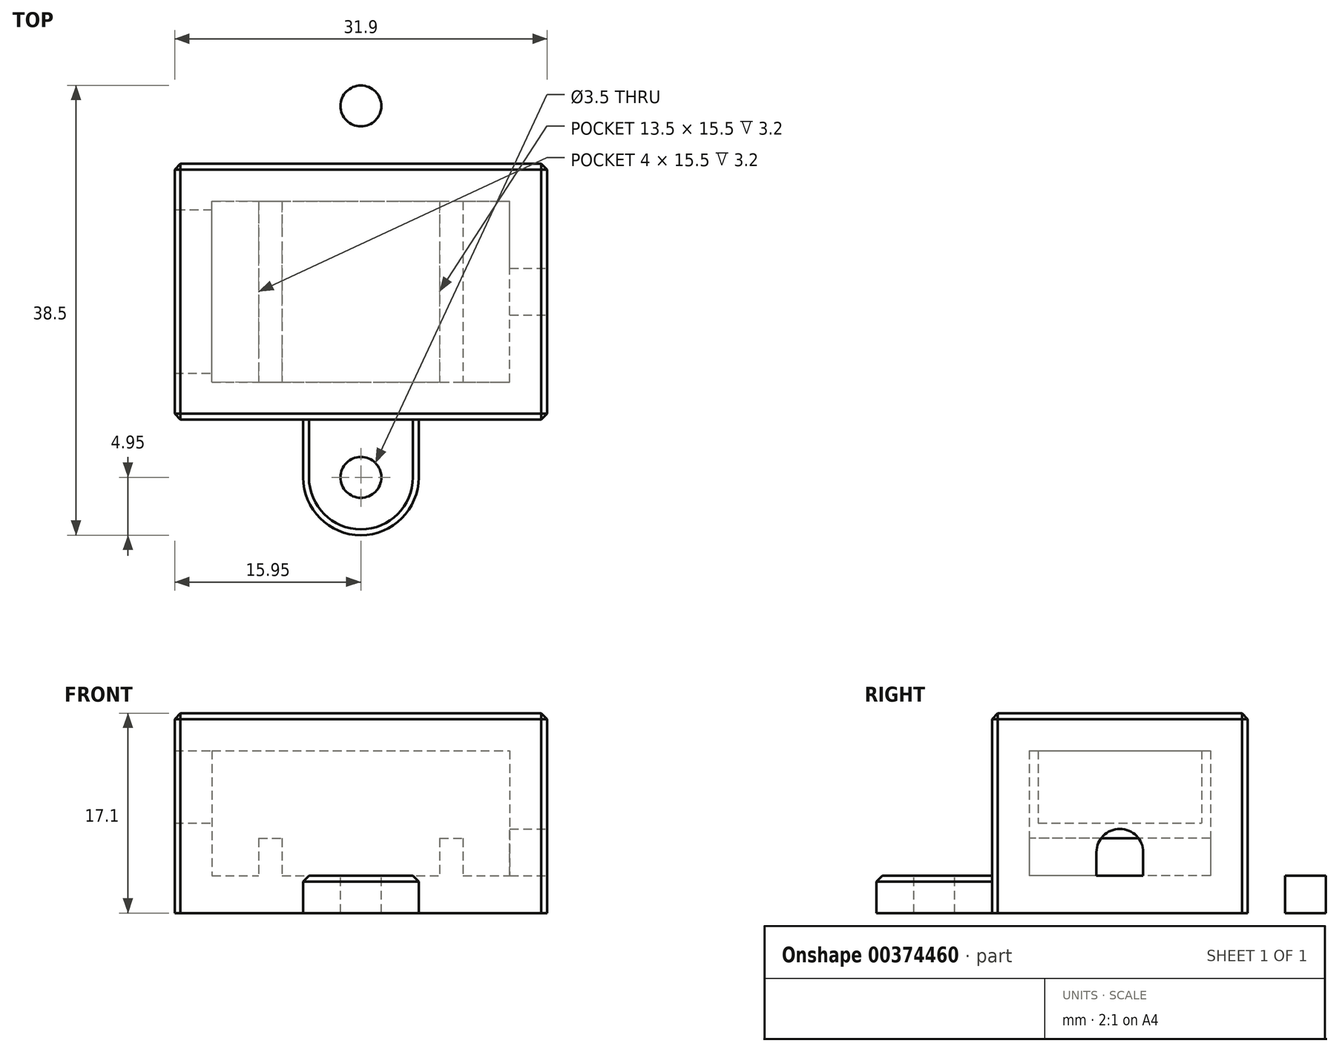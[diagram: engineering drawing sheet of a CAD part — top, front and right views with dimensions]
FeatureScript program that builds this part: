
annotation { "Feature Type Name" : "Feature", "Feature Type Description" : "" }
export const myFeature = defineFeature(function(context is Context, id is Id, definition is map)
    precondition{}
    {
        {
            assignVariable(context, id + "F0", {"name" : "mod_height", "anyValue" : 7.5});
        }
        {
            assignVariable(context, id + "F1", {"name" : "wall", "anyValue" : 3.2});
        }
        {
            var Q0;
            Q0=qCreatedBy(makeId("Top.planeOp"),FACE);
            var sketch = newSketch(context, id + "F2", { "sketchPlane" : qUnion([Q0])});
            skLineSegment(sketch, "E0.bottom", {"start": v(3.2, 3.2) * mm, "end": v(28.7, 3.2) * mm});
            skLineSegment(sketch, "E0.top", {"start": v(3.2, 18.7) * mm, "end": v(28.7, 18.7) * mm});
            skLineSegment(sketch, "E0.left", {"start": v(3.2, 3.2) * mm, "end": v(3.2, 18.7) * mm});
            skLineSegment(sketch, "E0.right", {"start": v(28.7, 3.2) * mm, "end": v(28.7, 18.7) * mm});
            skLineSegment(sketch, "E1", {"start": v(7.2, 18.7) * mm, "end": v(7.2, 3.2) * mm});
            skLineSegment(sketch, "E2", {"start": v(9.2, 18.7) * mm, "end": v(9.2, 3.2) * mm});
            skLineSegment(sketch, "E3", {"start": v(22.7, 18.7) * mm, "end": v(22.7, 3.2) * mm});
            skLineSegment(sketch, "E4", {"start": v(24.7, 18.7) * mm, "end": v(24.7, 3.2) * mm});
            skLineSegment(sketch, "E5.0", {"start": v(0, 21.9) * mm, "end": v(31.9, 21.9) * mm});
            skLineSegment(sketch, "E5.1", {"start": v(0, 0) * mm, "end": v(0, 21.9) * mm});
            skLineSegment(sketch, "E5.2", {"start": v(0, 0) * mm, "end": v(31.9, 0) * mm});
            skLineSegment(sketch, "E5.3", {"start": v(31.9, 0) * mm, "end": v(31.9, 21.9) * mm});
            skLineSegment(sketch, "E6", {"start": v(3.2, 17.95) * mm, "end": v(0, 17.95) * mm});
            skLineSegment(sketch, "E7", {"start": v(0, 3.95) * mm, "end": v(3.2, 3.95) * mm});
            skLineSegment(sketch, "E8.0", {"start": v(1.6, 1.6) * mm, "end": v(30.3, 1.6) * mm});
            skLineSegment(sketch, "E8.1", {"start": v(1.6, 1.6) * mm, "end": v(1.6, 20.3) * mm});
            skLineSegment(sketch, "E8.2", {"start": v(1.6, 20.3) * mm, "end": v(30.3, 20.3) * mm});
            skLineSegment(sketch, "E8.3", {"start": v(30.3, 1.6) * mm, "end": v(30.3, 20.3) * mm});
            skCircle(sketch, "E9", {"center": v(15.95, -4.95) * mm, "radius": 1.75 * mm});
            skArc(sketch, "E10", {"start": v(11, -4.95) * mm, "mid": v(15.95, -9.9) * mm, "end": v(20.9, -4.95) * mm});
            skLineSegment(sketch, "E11", {"start": v(11, -4.95) * mm, "end": v(11, 0) * mm});
            skLineSegment(sketch, "E12", {"start": v(20.9, -4.95) * mm, "end": v(20.9, 0) * mm});
            skPoint(sketch, "E13", {"position": v(15.95, 0) * mm});
            skLineSegment(sketch, "E14", {"start": v(0, 10.95) * mm, "end": v(31.9, 10.95) * mm, "construction": true});
            skCircle(sketch, "E15.MirrorC", {"center": v(15.95, 26.85) * mm, "radius": 1.75 * mm});
            skLineSegment(sketch, "E16.MirrorCS", {"start": v(20.9, 26.85) * mm, "end": v(20.9, 21.9) * mm});
            skLineSegment(sketch, "E17.MirrorCS", {"start": v(11, 26.85) * mm, "end": v(11, 21.9) * mm});
            skArc(sketch, "E18.MirrorCS", {"start": v(11, 26.85) * mm, "mid": v(15.95, 31.8) * mm, "end": v(20.9, 26.85) * mm});
            skSolve(sketch);
        }
        {
            var Q0;
            {var subQ0=sQuery(id+"F2.wireOp",EDGE,"E0.right");Q0=makeQuery(id+"F2.imprint","IMPRINT",FACE,{"disambiguationData":[TD([[makeQuery(id+"F2.imprint","IMPRINT",EDGE,{"derivedFrom":subQ0}),-1.0]])]});}
            var Q1;
            {var subQ5=sQuery(id+"F2.wireOp",EDGE,"E1");Q1=makeQuery(id+"F2.imprint","IMPRINT",FACE,{"disambiguationData":[TD([[makeQuery(id+"F2.imprint","IMPRINT",EDGE,{"derivedFrom":subQ5}),-1.0]])]});}
            var Q2;
            {var subQ0=sQuery(id+"F2.wireOp",EDGE,"E3");Q2=makeQuery(id+"F2.imprint","IMPRINT",FACE,{"disambiguationData":[TD([[makeQuery(id+"F2.imprint","IMPRINT",EDGE,{"derivedFrom":subQ0}),1.0]])]});}
            var Q3;
            {var subQ0=sQuery(id+"F2.wireOp",EDGE,"E2");Q3=makeQuery(id+"F2.imprint","IMPRINT",FACE,{"disambiguationData":[TD([[makeQuery(id+"F2.imprint","IMPRINT",EDGE,{"derivedFrom":subQ0}),1.0]])]});}
            var Q4;
            {var subQ0=sQuery(id+"F2.wireOp",EDGE,"E6");Q4=makeQuery(id+"F2.imprint","IMPRINT",FACE,{"disambiguationData":[TD([[makeQuery(id+"F2.imprint","IMPRINT",EDGE,{"derivedFrom":subQ0}),1.0]])]});}
            var Q5;
            {var subQ0=sQuery(id+"F2.wireOp",EDGE,"E0.right");Q5=makeQuery(id+"F2.imprint","IMPRINT",FACE,{"disambiguationData":[TD([[makeQuery(id+"F2.imprint","IMPRINT",EDGE,{"derivedFrom":subQ0}),1.0]])]});}
            var Q6;
            {var subQ0=sQuery(id+"F2.wireOp",EDGE,"E1");Q6=makeQuery(id+"F2.imprint","IMPRINT",FACE,{"disambiguationData":[TD([[makeQuery(id+"F2.imprint","IMPRINT",EDGE,{"derivedFrom":subQ0}),1.0]])]});}
            var Q7;
            {var subQ10=sQuery(id+"F2.wireOp",EDGE,"E5.0");Q7=makeQuery(id+"F2.imprint","IMPRINT",FACE,{"disambiguationData":[TD([[makeQuery(id+"F2.imprint","IMPRINT",EDGE,{"derivedFrom":subQ10}),-1.0]])]});}
            var Q8;
            Q8=makeQuery(id+"F2.imprint","IMPRINT",FACE,{"disambiguationData":[TD([[makeQuery(id+"F2.imprint","IMPRINT",EDGE,{"derivedFrom":sQuery(id+"F2.wireOp",EDGE,"E15.MirrorC")}),1.0]])]});
            var Q9;
            Q9=makeQuery(id+"F2.imprint","IMPRINT",FACE,{"disambiguationData":[TD([[makeQuery(id+"F2.imprint","IMPRINT",EDGE,{"derivedFrom":sQuery(id+"F2.wireOp",EDGE,"E9")}),-1.0]])]});
            var Q10;
            Q10=sQuery(id+"F2.wireOp",EDGE,"E5.0");
            var Q11;
            Q11=sQuery(id+"F2.wireOp",EDGE,"E5.3");
            var Q12;
            Q12=sQuery(id+"F2.wireOp",EDGE,"E5.2");
            var Q13;
            Q13=sQuery(id+"F2.wireOp",EDGE,"E5.1");
            extrude(context, id + "F3", {"entities" : qUnion([Q0, Q1, Q2, Q3, Q4, Q5, Q6, Q7, Q8, Q9]), "surfaceEntities" : qUnion([Q10, Q11, Q12, Q13]), "oppositeDirection" : true, "depth" : (getVariable(context, 'wall')) * mm});
        }
        {
            var Q0;
            {var subQ0=sQuery(id+"F2.wireOp",EDGE,"E1");Q0=makeQuery(id+"F2.imprint","IMPRINT",FACE,{"disambiguationData":[TD([[makeQuery(id+"F2.imprint","IMPRINT",EDGE,{"derivedFrom":subQ0}),1.0]])]});}
            var Q1;
            {var subQ0=sQuery(id+"F2.wireOp",EDGE,"E3");Q1=makeQuery(id+"F2.imprint","IMPRINT",FACE,{"disambiguationData":[TD([[makeQuery(id+"F2.imprint","IMPRINT",EDGE,{"derivedFrom":subQ0}),1.0]])]});}
            var Q2;
            Q2=makeQuery(id+"F3.opExtrude","CAP_FACE",FACE,{"disambiguationData":[OSD([sQuery(id+"F2.wireOp",EDGE,"E5.0"),sQuery(id+"F2.wireOp",EDGE,"E5.1"),sQuery(id+"F2.wireOp",EDGE,"E5.2"),sQuery(id+"F2.wireOp",EDGE,"E5.3")])],"isStart":false});
            extrude(context, id + "F4", {"entities" : qUnion([Q0, Q1]), "operationType" : NewBodyOperationType.ADD, "depth" : (getVariable(context, 'wall')) * mm});
        }
        {
            var Q0;
            {var subQ0=sQuery(id+"F2.wireOp",EDGE,"E6");var subQ1=sQuery(id+"F2.wireOp",EDGE,"E5.1");var subQ2=makeQuery(id+"F2.imprint","INTERSECT",VERTEX,{"derivedFrom":[subQ1,subQ0]});Q0=makeQuery(id+"F2.imprint","IMPRINT",FACE,{"disambiguationData":[TD([[makeQuery(id+"F2.imprint","IMPRINT",EDGE,{"disambiguationData":[TD([[subQ2,1.0]])],"derivedFrom":subQ1}),-1.0]])]});}
            var Q1;
            {var subQ0=sQuery(id+"F2.wireOp",EDGE,"E6");var subQ1=sQuery(id+"F2.wireOp",EDGE,"E0.left");var subQ2=makeQuery(id+"F2.imprint","INTERSECT",VERTEX,{"derivedFrom":[subQ1,subQ0]});Q1=makeQuery(id+"F2.imprint","IMPRINT",FACE,{"disambiguationData":[TD([[makeQuery(id+"F2.imprint","IMPRINT",EDGE,{"disambiguationData":[TD([[subQ2,1.0]])],"derivedFrom":subQ1}),1.0]])]});}
            extrude(context, id + "F5", {"entities" : qUnion([Q0, Q1]), "operationType" : NewBodyOperationType.ADD, "depth" : (getVariable(context, 'wall') + 1.3) * mm});
        }
        {
            var Q0;
            {var subQ0=sQuery(id+"F2.wireOp",EDGE,"E0.right");Q0=makeQuery(id+"F2.imprint","IMPRINT",FACE,{"disambiguationData":[TD([[makeQuery(id+"F2.imprint","IMPRINT",EDGE,{"derivedFrom":subQ0}),-1.0]])]});}
            extrude(context, id + "F6", {"entities" : qUnion([Q0]), "operationType" : NewBodyOperationType.ADD, "depth" : (getVariable(context, 'mod_height') + getVariable(context, 'wall')) * mm});
        }
        {
            var Q0;
            {var subQ10=sQuery(id+"F2.wireOp",EDGE,"E5.0");Q0=makeQuery(id+"F2.imprint","IMPRINT",FACE,{"disambiguationData":[TD([[makeQuery(id+"F2.imprint","IMPRINT",EDGE,{"derivedFrom":subQ10}),-1.0]])]});}
            extrude(context, id + "F7", {"entities" : qUnion([Q0]), "depth" : (getVariable(context, 'wall') + getVariable(context, 'mod_height')) * mm});
        }
        {
            var Q0;
            {var subQ0=sQuery(id+"F2.wireOp",EDGE,"E6");var subQ1=sQuery(id+"F2.wireOp",EDGE,"E5.1");var subQ2=makeQuery(id+"F2.imprint","INTERSECT",VERTEX,{"derivedFrom":[subQ1,subQ0]});Q0=makeQuery(id+"F2.imprint","IMPRINT",FACE,{"disambiguationData":[TD([[makeQuery(id+"F2.imprint","IMPRINT",EDGE,{"disambiguationData":[TD([[subQ2,1.0]])],"derivedFrom":subQ1}),-1.0]])]});}
            var Q1;
            {var subQ0=sQuery(id+"F2.wireOp",EDGE,"E5.3");Q1=makeQuery(id+"F2.imprint","IMPRINT",FACE,{"disambiguationData":[TD([[makeQuery(id+"F2.imprint","IMPRINT",EDGE,{"derivedFrom":subQ0}),1.0]])]});}
            var Q2;
            {var subQ0=sQuery(id+"F2.wireOp",EDGE,"E1");Q2=makeQuery(id+"F2.imprint","IMPRINT",FACE,{"disambiguationData":[TD([[makeQuery(id+"F2.imprint","IMPRINT",EDGE,{"derivedFrom":subQ0}),1.0]])]});}
            var Q3;
            {var subQ0=sQuery(id+"F2.wireOp",EDGE,"E2");Q3=makeQuery(id+"F2.imprint","IMPRINT",FACE,{"disambiguationData":[TD([[makeQuery(id+"F2.imprint","IMPRINT",EDGE,{"derivedFrom":subQ0}),1.0]])]});}
            var Q4;
            {var subQ0=sQuery(id+"F2.wireOp",EDGE,"E3");Q4=makeQuery(id+"F2.imprint","IMPRINT",FACE,{"disambiguationData":[TD([[makeQuery(id+"F2.imprint","IMPRINT",EDGE,{"derivedFrom":subQ0}),1.0]])]});}
            var Q5;
            {var subQ0=sQuery(id+"F2.wireOp",EDGE,"E0.right");Q5=makeQuery(id+"F2.imprint","IMPRINT",FACE,{"disambiguationData":[TD([[makeQuery(id+"F2.imprint","IMPRINT",EDGE,{"derivedFrom":subQ0}),-1.0]])]});}
            var Q6;
            {var subQ0=sQuery(id+"F2.wireOp",EDGE,"E0.right");Q6=makeQuery(id+"F2.imprint","IMPRINT",FACE,{"disambiguationData":[TD([[makeQuery(id+"F2.imprint","IMPRINT",EDGE,{"derivedFrom":subQ0}),1.0]])]});}
            var Q7;
            {var subQ5=sQuery(id+"F2.wireOp",EDGE,"E1");Q7=makeQuery(id+"F2.imprint","IMPRINT",FACE,{"disambiguationData":[TD([[makeQuery(id+"F2.imprint","IMPRINT",EDGE,{"derivedFrom":subQ5}),-1.0]])]});}
            var Q8;
            {var subQ0=sQuery(id+"F2.wireOp",EDGE,"E6");var subQ1=sQuery(id+"F2.wireOp",EDGE,"E0.left");var subQ2=makeQuery(id+"F2.imprint","INTERSECT",VERTEX,{"derivedFrom":[subQ1,subQ0]});Q8=makeQuery(id+"F2.imprint","IMPRINT",FACE,{"disambiguationData":[TD([[makeQuery(id+"F2.imprint","IMPRINT",EDGE,{"disambiguationData":[TD([[subQ2,1.0]])],"derivedFrom":subQ1}),1.0]])]});}
            var Q9;
            Q9=makeQuery(id+"F7.opExtrude","CAP_FACE",FACE,{"disambiguationData":[OSD([sQuery(id+"F2.wireOp",EDGE,"E5.0"),sQuery(id+"F2.wireOp",EDGE,"E5.1"),sQuery(id+"F2.wireOp",EDGE,"E5.2"),sQuery(id+"F2.wireOp",EDGE,"E5.3"),sQuery(id+"F2.wireOp",EDGE,"E6"),sQuery(id+"F2.wireOp",EDGE,"E7"),sQuery(id+"F2.wireOp",EDGE,"E8.0"),sQuery(id+"F2.wireOp",EDGE,"E8.1"),sQuery(id+"F2.wireOp",EDGE,"E8.2"),sQuery(id+"F2.wireOp",EDGE,"E8.3")])],"isStart":false});
            extrude(context, id + "F8", {"entities" : qUnion([Q0, Q1, Q2, Q3, Q4, Q5, Q6, Q7, Q8]), "operationType" : NewBodyOperationType.ADD, "depth" : (getVariable(context, 'wall') + getVariable(context, 'mod_height') + getVariable(context, 'wall')) * mm, "hasSecondDirection" : true, "secondDirectionBound" : SecondDirectionBoundingType.UP_TO_SURFACE, "secondDirectionOppositeDirection" : false, "secondDirectionBoundEntityFace" : qUnion([Q9]), "secondDirectionDepth" : 9.7 * mm});
        }
        {
            var Q0;
            {var subQ0=sQuery(id+"F2.wireOp",EDGE,"E5.3");Q0=makeQuery(id+"F8.boolean.opBoolean","MERGE",FACE,{"derivedFrom":[makeQuery(id+"F7.opExtrude","SWEPT_FACE",FACE,{"disambiguationData":[OSD([subQ0])]}),makeQuery(id+"F8.opExtrude","SWEPT_FACE",FACE,{"disambiguationData":[OSD([subQ0])]})]});}
            var sketch = newSketch(context, id + "F9", { "sketchPlane" : qUnion([Q0])});
            skArc(sketch, "E19", {"start": v(12.95, 2) * mm, "mid": v(10.95, 4) * mm, "end": v(8.95, 2) * mm});
            skLineSegment(sketch, "E20", {"start": v(8.95, 2) * mm, "end": v(8.95, 0) * mm});
            skLineSegment(sketch, "E21", {"start": v(8.95, 0) * mm, "end": v(12.95, 0) * mm});
            skLineSegment(sketch, "E22", {"start": v(12.95, 0) * mm, "end": v(12.95, 2) * mm});
            skSolve(sketch);
        }
        {
            var Q0;
            Q0=makeQuery(id+"F9.imprint","IMPRINT",FACE,{"disambiguationData":[TD([[makeQuery(id+"F9.imprint","IMPRINT",EDGE,{"derivedFrom":sQuery(id+"F9.wireOp",EDGE,"E19")}),1.0]])]});
            var Q1;
            Q1=makeQuery(id+"F6.opExtrude","SWEPT_FACE",FACE,{"disambiguationData":[OSD([sQuery(id+"F2.wireOp",EDGE,"E0.right")])]});
            extrude(context, id + "F10", {"entities" : qUnion([Q0]), "operationType" : NewBodyOperationType.REMOVE, "endBound" : BoundingType.UP_TO_SURFACE, "oppositeDirection" : true, "endBoundEntityFace" : qUnion([Q1]), "depth" : 25 * mm});
        }
        {
            var Q0;
            Q0=makeQuery(id+"F8.opExtrude","CAP_FACE",FACE,{"disambiguationData":[OSD([sQuery(id+"F2.wireOp",EDGE,"E5.0"),sQuery(id+"F2.wireOp",EDGE,"E5.1"),sQuery(id+"F2.wireOp",EDGE,"E5.2"),sQuery(id+"F2.wireOp",EDGE,"E5.3")])],"isStart":false});
            var Q1;
            {var subQ0=sQuery(id+"F2.wireOp",EDGE,"E5.1");var subQ1=sQuery(id+"F2.wireOp",EDGE,"E5.0");Q1=makeQuery(id+"F8.boolean.opBoolean","MERGE",EDGE,{"derivedFrom":[makeQuery(id+"F7.opExtrude","SWEPT_EDGE",EDGE,{"disambiguationData":[OSD([subQ1,subQ0])]}),makeQuery(id+"F8.opExtrude","SWEPT_EDGE",EDGE,{"disambiguationData":[OSD([subQ1,subQ0])]})]});}
            var Q2;
            Q2=makeQuery(id+"F3.opExtrude","SWEPT_EDGE",EDGE,{"disambiguationData":[OSD([sQuery(id+"F2.wireOp",EDGE,"E5.0"),sQuery(id+"F2.wireOp",EDGE,"E5.1")])]});
            var Q3;
            Q3=makeQuery(id+"F3.opExtrude","SWEPT_EDGE",EDGE,{"disambiguationData":[OSD([sQuery(id+"F2.wireOp",EDGE,"E5.1"),sQuery(id+"F2.wireOp",EDGE,"E5.2")])]});
            var Q4;
            {var subQ0=sQuery(id+"F2.wireOp",EDGE,"E5.2");var subQ1=sQuery(id+"F2.wireOp",EDGE,"E5.1");Q4=makeQuery(id+"F8.boolean.opBoolean","MERGE",EDGE,{"derivedFrom":[makeQuery(id+"F7.opExtrude","SWEPT_EDGE",EDGE,{"disambiguationData":[OSD([subQ1,subQ0])]}),makeQuery(id+"F8.opExtrude","SWEPT_EDGE",EDGE,{"disambiguationData":[OSD([subQ1,subQ0])]})]});}
            var Q5;
            {var subQ0=sQuery(id+"F2.wireOp",EDGE,"E5.3");var subQ1=sQuery(id+"F2.wireOp",EDGE,"E5.2");Q5=makeQuery(id+"F8.boolean.opBoolean","MERGE",EDGE,{"derivedFrom":[makeQuery(id+"F7.opExtrude","SWEPT_EDGE",EDGE,{"disambiguationData":[OSD([subQ1,subQ0])]}),makeQuery(id+"F8.opExtrude","SWEPT_EDGE",EDGE,{"disambiguationData":[OSD([subQ1,subQ0])]})]});}
            var Q6;
            Q6=makeQuery(id+"F3.opExtrude","SWEPT_EDGE",EDGE,{"disambiguationData":[OSD([sQuery(id+"F2.wireOp",EDGE,"E5.2"),sQuery(id+"F2.wireOp",EDGE,"E5.3")])]});
            var Q7;
            {var subQ0=sQuery(id+"F2.wireOp",EDGE,"E5.3");var subQ1=sQuery(id+"F2.wireOp",EDGE,"E5.0");Q7=makeQuery(id+"F8.boolean.opBoolean","MERGE",EDGE,{"derivedFrom":[makeQuery(id+"F7.opExtrude","SWEPT_EDGE",EDGE,{"disambiguationData":[OSD([subQ1,subQ0])]}),makeQuery(id+"F8.opExtrude","SWEPT_EDGE",EDGE,{"disambiguationData":[OSD([subQ1,subQ0])]})]});}
            var Q8;
            Q8=makeQuery(id+"F3.opExtrude","SWEPT_EDGE",EDGE,{"disambiguationData":[OSD([sQuery(id+"F2.wireOp",EDGE,"E5.0"),sQuery(id+"F2.wireOp",EDGE,"E5.3")])]});
            var Q9;
            Q9=makeQuery(id+"F3.opExtrude","CAP_EDGE",EDGE,{"disambiguationData":[OSD([sQuery(id+"F2.wireOp",EDGE,"E18.MirrorCS")])],"isStart":true});
            var Q10;
            Q10=makeQuery(id+"F3.opExtrude","CAP_EDGE",EDGE,{"disambiguationData":[OSD([sQuery(id+"F2.wireOp",EDGE,"E10")])],"isStart":true});
            var Q11;
            Q11=makeQuery(id+"F10.boolean.opBoolean","COPY",EDGE,{"derivedFrom":makeQuery(id+"F10.opExtrude","CAP_EDGE",EDGE,{"disambiguationData":[OSD([sQuery(id+"F9.wireOp",EDGE,"E22")])],"isStart":true})});
            chamfer(context, id + "F11", {"entities" : qUnion([Q0, Q1, Q2, Q3, Q4, Q5, Q6, Q7, Q8, Q9, Q10, Q11]), "width" : .5 * mm, "tangentPropagation" : true});
        }
    });
